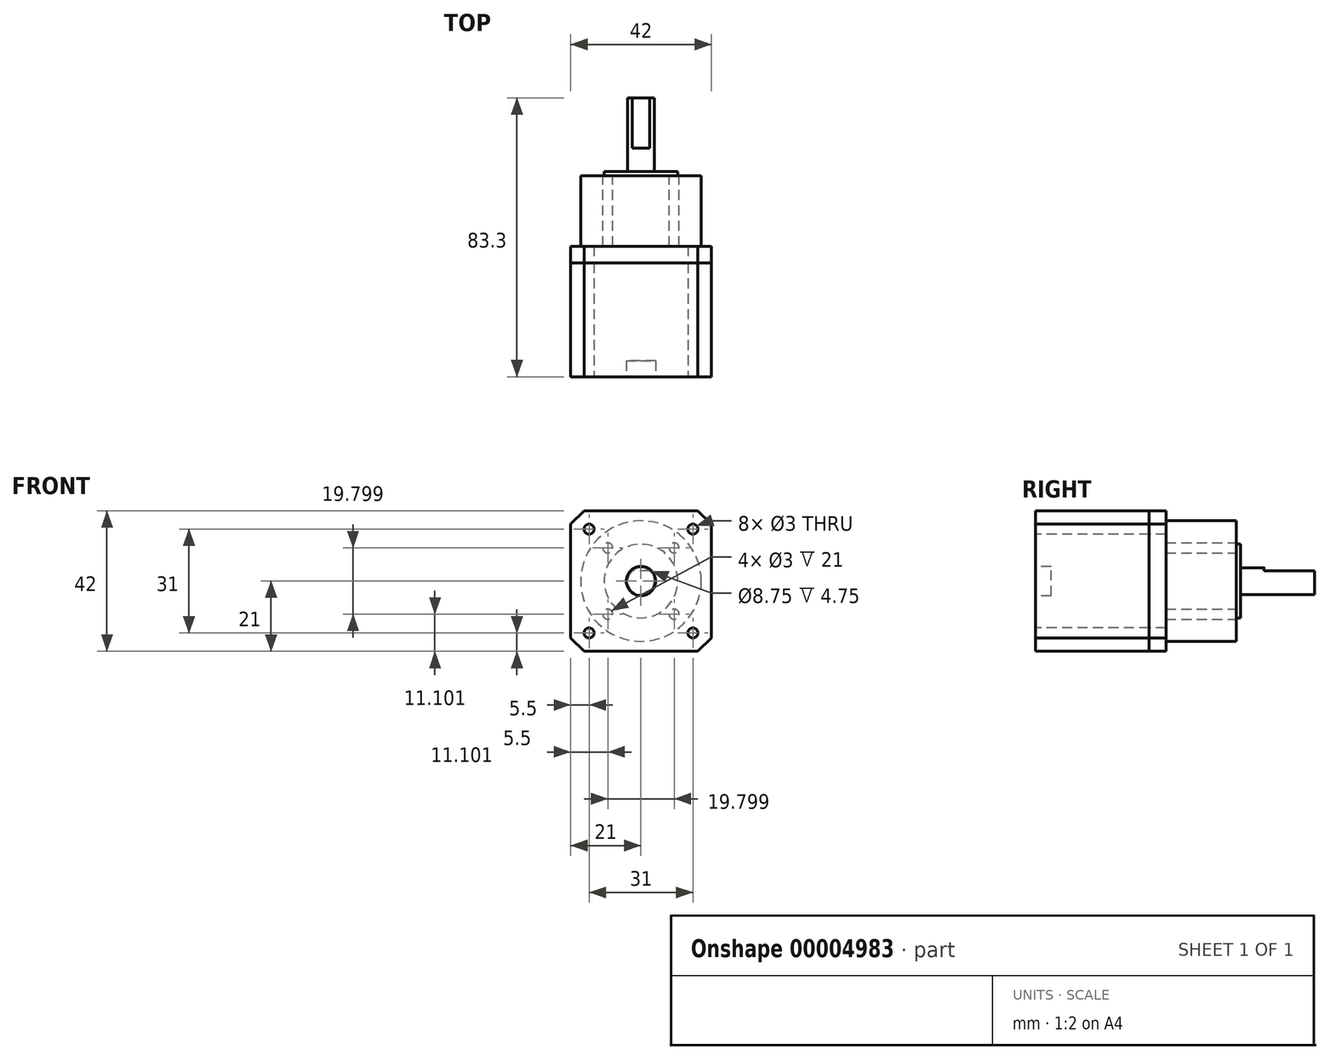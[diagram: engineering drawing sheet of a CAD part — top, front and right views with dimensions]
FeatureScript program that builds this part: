
annotation { "Feature Type Name" : "Feature", "Feature Type Description" : "" }
export const myFeature = defineFeature(function(context is Context, id is Id, definition is map)
    precondition{}
    {
        {
            var Q0;
            Q0=qCreatedBy(makeId("Front.planeOp"),FACE);
            var sketch = newSketch(context, id + "F0", { "sketchPlane" : qUnion([Q0])});
            skLineSegment(sketch, "E0.rect.bottom", {"start": v(21, 21) * mm, "end": v(-21, 21) * mm});
            skLineSegment(sketch, "E0.rect.top", {"start": v(21, -21) * mm, "end": v(-21, -21) * mm});
            skLineSegment(sketch, "E0.rect.left", {"start": v(21, 21) * mm, "end": v(21, -21) * mm});
            skLineSegment(sketch, "E0.rect.right", {"start": v(-21, 21) * mm, "end": v(-21, -21) * mm});
            skPoint(sketch, "E0.rect.middle", {"position": v(0, 0) * mm});
            skSolve(sketch);
        }
        {
            var Q0;
            Q0 = qSketchRegion(id + "F0", true);
            extrude(context, id + "F1", {"entities" : qUnion([Q0]), "depth" : 34 * mm});
        }
        {
            var Q0;
            Q0=makeQuery(id+"F1.opExtrude","SWEPT_EDGE",EDGE,{"disambiguationData":[OSD([sQuery(id+"F0.wireOp",EDGE,"E0.rect.bottom"),sQuery(id+"F0.wireOp",EDGE,"E0.rect.left")])]});
            var Q1;
            Q1=makeQuery(id+"F1.opExtrude","SWEPT_EDGE",EDGE,{"disambiguationData":[OSD([sQuery(id+"F0.wireOp",EDGE,"E0.rect.bottom"),sQuery(id+"F0.wireOp",EDGE,"E0.rect.right")])]});
            var Q2;
            Q2=makeQuery(id+"F1.opExtrude","SWEPT_EDGE",EDGE,{"disambiguationData":[OSD([sQuery(id+"F0.wireOp",EDGE,"E0.rect.top"),sQuery(id+"F0.wireOp",EDGE,"E0.rect.left")])]});
            var Q3;
            Q3=makeQuery(id+"F1.opExtrude","SWEPT_EDGE",EDGE,{"disambiguationData":[OSD([sQuery(id+"F0.wireOp",EDGE,"E0.rect.top"),sQuery(id+"F0.wireOp",EDGE,"E0.rect.right")])]});
            chamfer(context, id + "F2", {"entities" : qUnion([Q0, Q1, Q2, Q3]), "width" : 4 * mm, "tangentPropagation" : true});
        }
        {
            var Q0;
            Q0=makeQuery(id+"F1.opExtrude","CAP_FACE",FACE,{"disambiguationData":[OSD([sQuery(id+"F0.wireOp",EDGE,"E0.rect.bottom"),sQuery(id+"F0.wireOp",EDGE,"E0.rect.top"),sQuery(id+"F0.wireOp",EDGE,"E0.rect.left"),sQuery(id+"F0.wireOp",EDGE,"E0.rect.right")])],"isStart":false});
            var sketch = newSketch(context, id + "F3", { "sketchPlane" : qUnion([Q0])});
            skCircle(sketch, "E1", {"center": v(0, 0) * mm, "radius": 4.38 * mm});
            skSolve(sketch);
        }
        {
            var Q0;
            Q0 = qSketchRegion(id + "F3", true);
            extrude(context, id + "F4", {"entities" : qUnion([Q0]), "operationType" : NewBodyOperationType.REMOVE, "oppositeDirection" : true, "depth" : 4.75 * mm});
        }
        {
            var Q0;
            Q0=makeQuery(id+"F1.opExtrude","CAP_FACE",FACE,{"disambiguationData":[OSD([sQuery(id+"F0.wireOp",EDGE,"E0.rect.bottom"),sQuery(id+"F0.wireOp",EDGE,"E0.rect.top"),sQuery(id+"F0.wireOp",EDGE,"E0.rect.left"),sQuery(id+"F0.wireOp",EDGE,"E0.rect.right")])],"isStart":false});
            var sketch = newSketch(context, id + "F5", { "sketchPlane" : qUnion([Q0])});
            skLineSegment(sketch, "E2.rect.bottom", {"start": v(15.5, 15.5) * mm, "end": v(-15.5, 15.5) * mm, "construction": true});
            skLineSegment(sketch, "E2.rect.top", {"start": v(15.5, -15.5) * mm, "end": v(-15.5, -15.5) * mm, "construction": true});
            skLineSegment(sketch, "E2.rect.left", {"start": v(15.5, 15.5) * mm, "end": v(15.5, -15.5) * mm, "construction": true});
            skLineSegment(sketch, "E2.rect.right", {"start": v(-15.5, 15.5) * mm, "end": v(-15.5, -15.5) * mm, "construction": true});
            skPoint(sketch, "E2.rect.middle", {"position": v(0, 0) * mm});
            skCircle(sketch, "E3", {"center": v(-15.5, 15.5) * mm, "radius": 1.5 * mm});
            skCircle(sketch, "E4", {"center": v(15.5, 15.5) * mm, "radius": 1.5 * mm});
            skCircle(sketch, "E5", {"center": v(15.5, -15.5) * mm, "radius": 1.5 * mm});
            skCircle(sketch, "E6", {"center": v(-15.5, -15.5) * mm, "radius": 1.5 * mm});
            skSolve(sketch);
        }
        {
            var Q0;
            Q0 = qSketchRegion(id + "F5", true);
            extrude(context, id + "F6", {"entities" : qUnion([Q0]), "operationType" : NewBodyOperationType.REMOVE, "endBound" : BoundingType.THROUGH_ALL, "oppositeDirection" : true, "depth" : 25 * mm});
        }
        {
            var Q0;
            Q0=makeQuery(id+"F1.opExtrude","CAP_FACE",FACE,{"disambiguationData":[OSD([sQuery(id+"F0.wireOp",EDGE,"E0.rect.bottom"),sQuery(id+"F0.wireOp",EDGE,"E0.rect.top"),sQuery(id+"F0.wireOp",EDGE,"E0.rect.left"),sQuery(id+"F0.wireOp",EDGE,"E0.rect.right")])],"isStart":true});
            var sketch = newSketch(context, id + "F7", { "sketchPlane" : qUnion([Q0])});
            skLineSegment(sketch, "E7.0", {"start": v(-17, 21) * mm, "end": v(-21, 17) * mm});
            skLineSegment(sketch, "E7.1", {"start": v(-17, 21) * mm, "end": v(17, 21) * mm});
            skLineSegment(sketch, "E7.2", {"start": v(21, 17) * mm, "end": v(17, 21) * mm});
            skLineSegment(sketch, "E7.3", {"start": v(21, 17) * mm, "end": v(21, -17) * mm});
            skLineSegment(sketch, "E7.4", {"start": v(17, -21) * mm, "end": v(21, -17) * mm});
            skLineSegment(sketch, "E7.5", {"start": v(-17, -21) * mm, "end": v(17, -21) * mm});
            skLineSegment(sketch, "E7.6", {"start": v(-21, -17) * mm, "end": v(-17, -21) * mm});
            skLineSegment(sketch, "E7.7", {"start": v(-21, 17) * mm, "end": v(-21, -17) * mm});
            skCircle(sketch, "E7.8", {"center": v(-15.5, 15.5) * mm, "radius": 1.5 * mm});
            skCircle(sketch, "E7.9", {"center": v(15.5, 15.5) * mm, "radius": 1.5 * mm});
            skCircle(sketch, "E7.10", {"center": v(15.5, -15.5) * mm, "radius": 1.5 * mm});
            skCircle(sketch, "E7.11", {"center": v(-15.5, -15.5) * mm, "radius": 1.5 * mm});
            skSolve(sketch);
        }
        {
            var Q0;
            Q0 = qSketchRegion(id + "F7", true);
            extrude(context, id + "F8", {"entities" : qUnion([Q0]), "depth" : 5 * mm});
        }
        {
            var Q0;
            Q0=makeQuery(id+"F8.opExtrude","CAP_FACE",FACE,{"disambiguationData":[OSD([sQuery(id+"F7.wireOp",EDGE,"E7.0"),sQuery(id+"F7.wireOp",EDGE,"E7.1"),sQuery(id+"F7.wireOp",EDGE,"E7.2"),sQuery(id+"F7.wireOp",EDGE,"E7.3"),sQuery(id+"F7.wireOp",EDGE,"E7.4"),sQuery(id+"F7.wireOp",EDGE,"E7.5"),sQuery(id+"F7.wireOp",EDGE,"E7.6"),sQuery(id+"F7.wireOp",EDGE,"E7.7"),sQuery(id+"F7.wireOp",EDGE,"E7.8"),sQuery(id+"F7.wireOp",EDGE,"E7.9"),sQuery(id+"F7.wireOp",EDGE,"E7.10"),sQuery(id+"F7.wireOp",EDGE,"E7.11")])],"isStart":false});
            var sketch = newSketch(context, id + "F9", { "sketchPlane" : qUnion([Q0])});
            skCircle(sketch, "E8", {"center": v(0, 0) * mm, "radius": 18 * mm});
            skSolve(sketch);
        }
        {
            var Q0;
            Q0 = qSketchRegion(id + "F9", true);
            extrude(context, id + "F10", {"entities" : qUnion([Q0]), "operationType" : NewBodyOperationType.ADD, "depth" : 21 * mm});
        }
        {
            var Q0;
            Q0=makeQuery(id+"F10.opExtrude","CAP_FACE",FACE,{"disambiguationData":[OSD([sQuery(id+"F9.wireOp",EDGE,"E8")])],"isStart":false});
            var sketch = newSketch(context, id + "F11", { "sketchPlane" : qUnion([Q0])});
            skCircle(sketch, "E9", {"center": v(0, 0) * mm, "radius": 11 * mm});
            skSolve(sketch);
        }
        {
            var Q0;
            Q0 = qSketchRegion(id + "F11", true);
            extrude(context, id + "F12", {"entities" : qUnion([Q0]), "operationType" : NewBodyOperationType.ADD, "depth" : 1.3 * mm});
        }
        {
            var Q0;
            Q0=makeQuery(id+"F12.opExtrude","CAP_FACE",FACE,{"disambiguationData":[OSD([sQuery(id+"F11.wireOp",EDGE,"E9")])],"isStart":false});
            var sketch = newSketch(context, id + "F13", { "sketchPlane" : qUnion([Q0])});
            skCircle(sketch, "E10", {"center": v(0, 0) * mm, "radius": 4 * mm});
            skSolve(sketch);
        }
        {
            var Q0;
            Q0 = qSketchRegion(id + "F13", true);
            extrude(context, id + "F14", {"entities" : qUnion([Q0]), "operationType" : NewBodyOperationType.ADD, "depth" : 22 * mm});
        }
        {
            var Q0;
            Q0=makeQuery(id+"F14.opExtrude","CAP_FACE",FACE,{"disambiguationData":[OSD([sQuery(id+"F13.wireOp",EDGE,"E10")])],"isStart":false});
            var sketch = newSketch(context, id + "F15", { "sketchPlane" : qUnion([Q0])});
            skLineSegment(sketch, "E11", {"start": v(-2.65, 3) * mm, "end": v(2.65, 3) * mm});
            skArc(sketch, "E12.0", {"start": v(2.65, 3) * mm, "mid": v(0, 4) * mm, "end": v(-2.65, 3) * mm});
            skPoint(sketch, "E13", {"position": v(0, 4) * mm});
            skSolve(sketch);
        }
        {
            var Q0;
            Q0 = qSketchRegion(id + "F15", true);
            extrude(context, id + "F16", {"entities" : qUnion([Q0]), "operationType" : NewBodyOperationType.REMOVE, "oppositeDirection" : true, "depth" : 15 * mm});
        }
        {
            var Q0;
            Q0=makeQuery(id+"F10.opExtrude","CAP_FACE",FACE,{"disambiguationData":[OSD([sQuery(id+"F9.wireOp",EDGE,"E8")])],"isStart":false});
            var sketch = newSketch(context, id + "F17", { "sketchPlane" : qUnion([Q0])});
            skLineSegment(sketch, "E14", {"start": v(0, 18) * mm, "end": v(0, 0) * mm, "construction": true});
            skLineSegment(sketch, "E15", {"start": v(0, 0) * mm, "end": v(-18, 0) * mm, "construction": true});
            skLineSegment(sketch, "E16", {"start": v(-18, 0) * mm, "end": v(0, 18) * mm, "construction": true});
            skLineSegment(sketch, "E17", {"start": v(-9, 9) * mm, "end": v(0, 0) * mm, "construction": true});
            skCircle(sketch, "E18", {"center": v(-9.9, 9.9) * mm, "radius": 1.5 * mm});
            skCircle(sketch, "E19.1.0", {"center": v(-9.9, -9.9) * mm, "radius": 1.5 * mm});
            skCircle(sketch, "E19.2.0", {"center": v(9.9, -9.9) * mm, "radius": 1.5 * mm});
            skCircle(sketch, "E19.3.0", {"center": v(9.9, 9.9) * mm, "radius": 1.5 * mm});
            skPoint(sketch, "E19.center", {"position": v(0, 0) * mm});
            skSolve(sketch);
        }
        {
            var Q0;
            Q0 = qSketchRegion(id + "F17", true);
            var Q1;
            Q1=makeQuery(id+"F8.opExtrude","CAP_FACE",FACE,{"disambiguationData":[OSD([sQuery(id+"F7.wireOp",EDGE,"E7.0"),sQuery(id+"F7.wireOp",EDGE,"E7.1"),sQuery(id+"F7.wireOp",EDGE,"E7.2"),sQuery(id+"F7.wireOp",EDGE,"E7.3"),sQuery(id+"F7.wireOp",EDGE,"E7.4"),sQuery(id+"F7.wireOp",EDGE,"E7.5"),sQuery(id+"F7.wireOp",EDGE,"E7.6"),sQuery(id+"F7.wireOp",EDGE,"E7.7"),sQuery(id+"F7.wireOp",EDGE,"E7.8"),sQuery(id+"F7.wireOp",EDGE,"E7.9"),sQuery(id+"F7.wireOp",EDGE,"E7.10"),sQuery(id+"F7.wireOp",EDGE,"E7.11")])],"isStart":false});
            extrude(context, id + "F18", {"entities" : qUnion([Q0]), "operationType" : NewBodyOperationType.REMOVE, "endBound" : BoundingType.UP_TO_SURFACE, "oppositeDirection" : true, "endBoundEntityFace" : qUnion([Q1]), "depth" : 25 * mm});
        }
    });
